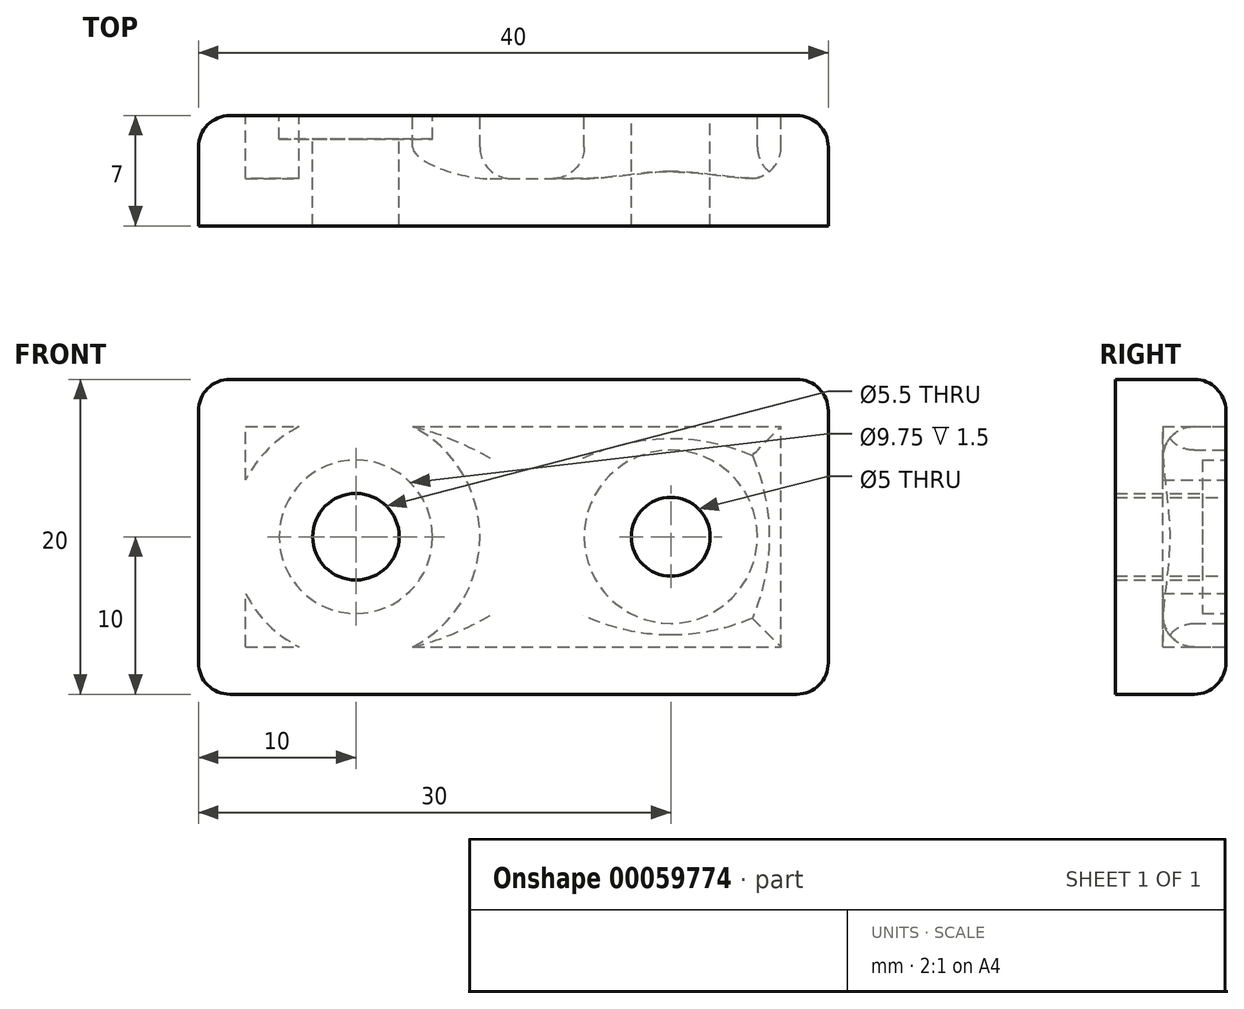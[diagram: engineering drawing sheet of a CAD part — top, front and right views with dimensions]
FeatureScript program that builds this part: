
annotation { "Feature Type Name" : "Feature", "Feature Type Description" : "" }
export const myFeature = defineFeature(function(context is Context, id is Id, definition is map)
    precondition{}
    {
        {
            var Q0;
            Q0=qCreatedBy(makeId("Front.planeOp"),FACE);
            var sketch = newSketch(context, id + "F0", { "sketchPlane" : qUnion([Q0])});
            skLineSegment(sketch, "E0.bottom", {"start": v(0, 0) * mm, "end": v(40, 0) * mm});
            skLineSegment(sketch, "E0.top", {"start": v(0, 20) * mm, "end": v(40, 20) * mm});
            skLineSegment(sketch, "E0.left", {"start": v(0, 0) * mm, "end": v(0, 20) * mm});
            skLineSegment(sketch, "E0.right", {"start": v(40, 0) * mm, "end": v(40, 20) * mm});
            skCircle(sketch, "E1", {"center": v(10, 10) * mm, "radius": 2.5 * mm});
            skPoint(sketch, "E1.centerSnap0", {"position": v(0, 10) * mm});
            skCircle(sketch, "E2", {"center": v(30, 10) * mm, "radius": 2.5 * mm});
            skSolve(sketch);
        }
        {
            var Q0;
            Q0=makeQuery(id+"F0.imprint","IMPRINT",FACE,{"disambiguationData":[TD([[makeQuery(id+"F0.imprint","IMPRINT",EDGE,{"derivedFrom":sQuery(id+"F0.wireOp",EDGE,"E0.bottom")}),1.0]])]});
            var Q1;
            Q1=makeQuery(id+"F0.imprint","IMPRINT",FACE,{"disambiguationData":[TD([[makeQuery(id+"F0.imprint","IMPRINT",EDGE,{"derivedFrom":sQuery(id+"F0.wireOp",EDGE,"E2")}),1.0]])]});
            var Q2;
            Q2=makeQuery(id+"F0.imprint","IMPRINT",FACE,{"disambiguationData":[TD([[makeQuery(id+"F0.imprint","IMPRINT",EDGE,{"derivedFrom":sQuery(id+"F0.wireOp",EDGE,"E1")}),1.0]])]});
            extrude(context, id + "F1", {"entities" : qUnion([Q0, Q1, Q2]), "depth" : 7 * mm});
        }
        {
            var Q0;
            Q0=makeQuery(id+"F1.opExtrude","CAP_FACE",FACE,{"disambiguationData":[OSD([sQuery(id+"F0.wireOp",EDGE,"E0.bottom"),sQuery(id+"F0.wireOp",EDGE,"E0.top"),sQuery(id+"F0.wireOp",EDGE,"E0.left"),sQuery(id+"F0.wireOp",EDGE,"E0.right")])],"isStart":true});
            var sketch = newSketch(context, id + "F2", { "sketchPlane" : qUnion([Q0])});
            skPoint(sketch, "E3.0", {"position": v(-10, 10) * mm});
            skPoint(sketch, "E4.0", {"position": v(-30, 10) * mm});
            skSolve(sketch);
        }
        {
            var Q0;
            Q0=sQuery(id+"F2.wireOp",VERTEX,"E3.0");
            var Q1;
            Q1=makeQuery(id+"F1.opExtrude","SWEPT_BODY",BODY,{"disambiguationData":[OSD([sQuery(id+"F0.wireOp",EDGE,"E0.bottom"),sQuery(id+"F0.wireOp",EDGE,"E0.top"),sQuery(id+"F0.wireOp",EDGE,"E0.left"),sQuery(id+"F0.wireOp",EDGE,"E0.right")])]});
            hole(context, id + "F3", {"style" : HoleStyle.C_BORE, "endStyle" : HoleEndStyle.BLIND, "holeDiameter" : 5.5 * mm, "cBoreDiameter" : 9.75 * mm, "cBoreDepth" : 1.5 * mm, "holeDepth" : 10 * mm, "startFromSketch" : true, "locations" : qUnion([Q0]), "scope" : qUnion([Q1])});
        }
        {
            var Q0;
            Q0=sQuery(id+"F2.wireOp",VERTEX,"E4.0");
            var Q1;
            Q1=makeQuery(id+"F1.opExtrude","SWEPT_BODY",BODY,{"disambiguationData":[OSD([sQuery(id+"F0.wireOp",EDGE,"E0.bottom"),sQuery(id+"F0.wireOp",EDGE,"E0.top"),sQuery(id+"F0.wireOp",EDGE,"E0.left"),sQuery(id+"F0.wireOp",EDGE,"E0.right")])]});
            hole(context, id + "F4", {"style" : HoleStyle.SIMPLE, "endStyle" : HoleEndStyle.THROUGH, "standardTappedOrClearance" : lookupTablePath({ "standard" : "ISO", "size" : "5", "type" : "Drilled" }), "standardBlindInLast" : lookupTablePath({ "standard" : "ISO", "size" : "5", "type" : "Drilled" }), "holeDiameter" : 5 * mm, "startFromSketch" : true, "locations" : qUnion([Q0]), "scope" : qUnion([Q1]), "isTappedThrough" : true});
        }
        {
            var Q0;
            Q0=makeQuery(id+"F1.opExtrude","CAP_FACE",FACE,{"disambiguationData":[OSD([sQuery(id+"F0.wireOp",EDGE,"E0.bottom"),sQuery(id+"F0.wireOp",EDGE,"E0.top"),sQuery(id+"F0.wireOp",EDGE,"E0.left"),sQuery(id+"F0.wireOp",EDGE,"E0.right")])],"isStart":true});
            shell(context, id + "F5", {"entities" : qUnion([Q0]), "thickness" : 3 * mm});
        }
        {
            var Q0;
            {var subQ0=sQuery(id+"F0.wireOp",EDGE,"E0.right");var subQ1=sQuery(id+"F0.wireOp",EDGE,"E0.left");var subQ2=sQuery(id+"F0.wireOp",EDGE,"E0.top");var subQ3=sQuery(id+"F0.wireOp",EDGE,"E0.bottom");Q0=makeQuery(id+"F5.opShell","OFFSET_FACE",FACE,{"disambiguationData":[OSD([subQ3,subQ2,subQ1,subQ0]),TDD([makeQuery(id+"F1.opExtrude","CAP_FACE",FACE,{"disambiguationData":[OSD([subQ3,subQ2,subQ1,subQ0])],"isStart":false})]),OD(0.0)]});}
            fillet(context, id + "F6", {"entities" : qUnion([Q0]), "radius" : 2 * mm, "tangentPropagation" : true, "allowEdgeOverflow" : false});
        }
        {
            var Q0;
            Q0=makeQuery(id+"F1.opExtrude","SWEPT_EDGE",EDGE,{"disambiguationData":[OSD([sQuery(id+"F0.wireOp",EDGE,"E0.top"),sQuery(id+"F0.wireOp",EDGE,"E0.right")])]});
            var Q1;
            Q1=makeQuery(id+"F1.opExtrude","SWEPT_EDGE",EDGE,{"disambiguationData":[OSD([sQuery(id+"F0.wireOp",EDGE,"E0.bottom"),sQuery(id+"F0.wireOp",EDGE,"E0.right")])]});
            var Q2;
            Q2=makeQuery(id+"F1.opExtrude","SWEPT_EDGE",EDGE,{"disambiguationData":[OSD([sQuery(id+"F0.wireOp",EDGE,"E0.top"),sQuery(id+"F0.wireOp",EDGE,"E0.left")])]});
            var Q3;
            Q3=makeQuery(id+"F1.opExtrude","SWEPT_EDGE",EDGE,{"disambiguationData":[OSD([sQuery(id+"F0.wireOp",EDGE,"E0.bottom"),sQuery(id+"F0.wireOp",EDGE,"E0.left")])]});
            var Q4;
            Q4=makeQuery(id+"F1.opExtrude","CAP_EDGE",EDGE,{"disambiguationData":[OSD([sQuery(id+"F0.wireOp",EDGE,"E0.bottom")])],"isStart":true});
            var Q5;
            Q5=makeQuery(id+"F1.opExtrude","CAP_EDGE",EDGE,{"disambiguationData":[OSD([sQuery(id+"F0.wireOp",EDGE,"E0.left")])],"isStart":true});
            var Q6;
            Q6=makeQuery(id+"F1.opExtrude","CAP_EDGE",EDGE,{"disambiguationData":[OSD([sQuery(id+"F0.wireOp",EDGE,"E0.top")])],"isStart":true});
            var Q7;
            Q7=makeQuery(id+"F1.opExtrude","CAP_EDGE",EDGE,{"disambiguationData":[OSD([sQuery(id+"F0.wireOp",EDGE,"E0.right")])],"isStart":true});
            fillet(context, id + "F7", {"entities" : qUnion([Q0, Q1, Q2, Q3, Q4, Q5, Q6, Q7]), "radius" : 2 * mm, "tangentPropagation" : true, "allowEdgeOverflow" : false});
        }
    });
